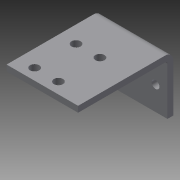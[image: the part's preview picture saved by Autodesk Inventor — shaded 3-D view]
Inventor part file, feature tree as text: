
AUTODESK INVENTOR PART (.ipt)
format: ipt  version: 2014 (Build 180170000, 170)  size: 126,976 bytes
history: native  units: in
note: dims shown in document units (in); Inventor stores cm internally (conversion verified against a paired STEP export)
features: sheet_metal_op x4, sketch x3, other x3
ambient origin geometry x8: Origin, YZ Plane, XZ Plane, XY Plane, X Axis, Y Axis, Z Axis, Center Point
bodies: Solid1 (feature_tree)
feature tree (10):
  sheet_metal_op  "Face1"
  sheet_metal_op  "Flange1"
  sketch  "Sketch1"  dims[d0=1.5in]
  other  "Plate1"
  sketch  "Sketch2"  dims[d1=1.0in]
  other  "Plate2"
  sheet_metal_op  "Bend1"
  sheet_metal_op  "Corner1"
  sketch  "Sketch3"  dims[d2=0.163in d3=0.5in d4=0.25in d5=0.7874in d7=1.0in d8=0.3937in d10=1.0in d12=0.125in d13=0.125in d14=0.0625in d15=0.25in d16=0.125in d17=2.0in d18=90.0deg d19=0.05in d20=0.5in d21=0.125in d22=0.125in d23=0.75in d24=1.31in d25=0.125in d26=0.22in d27=0.228in d28=0.5in d29=0.19in d30=0.125in d31=0.0in]
  other  "Cut1"
